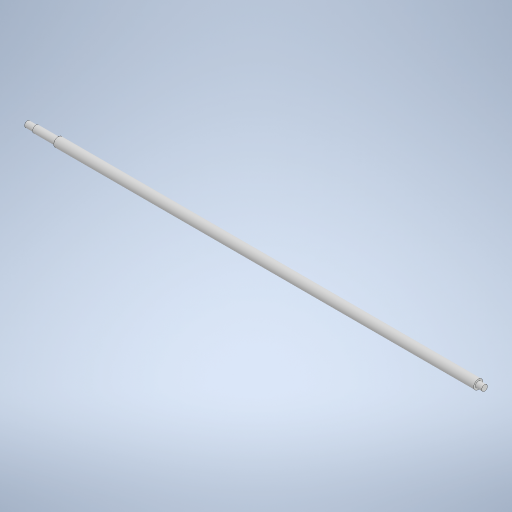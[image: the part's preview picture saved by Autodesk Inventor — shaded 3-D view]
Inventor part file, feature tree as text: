
AUTODESK INVENTOR PART (.ipt)
format: ipt  version: 2023 (Build 270158000, 158)  size: 249,856 bytes
history: native  units: mm
features: revolve x1, sketch x1
ambient origin geometry x8: Origin, YZ Plane, XZ Plane, XY Plane, X Axis, Y Axis, Z Axis, Center Point
bodies: Solid1 (feature_tree)
feature tree (2):
  revolve  "Revolution1"  [1 undecoded]
  sketch  "Sketch1"  dims[d0=5.0mm d1=6.0mm d2=8.0mm d3=5.0mm d4=11.0mm d6=39.0mm d8=15.0mm d9=800.0mm d10=90.0deg]
note: 1 required parameter value undecoded (feature->parameter linkage not recoverable at this tier; creation-order binding heuristic only, values carry confidence <= 0.55)
